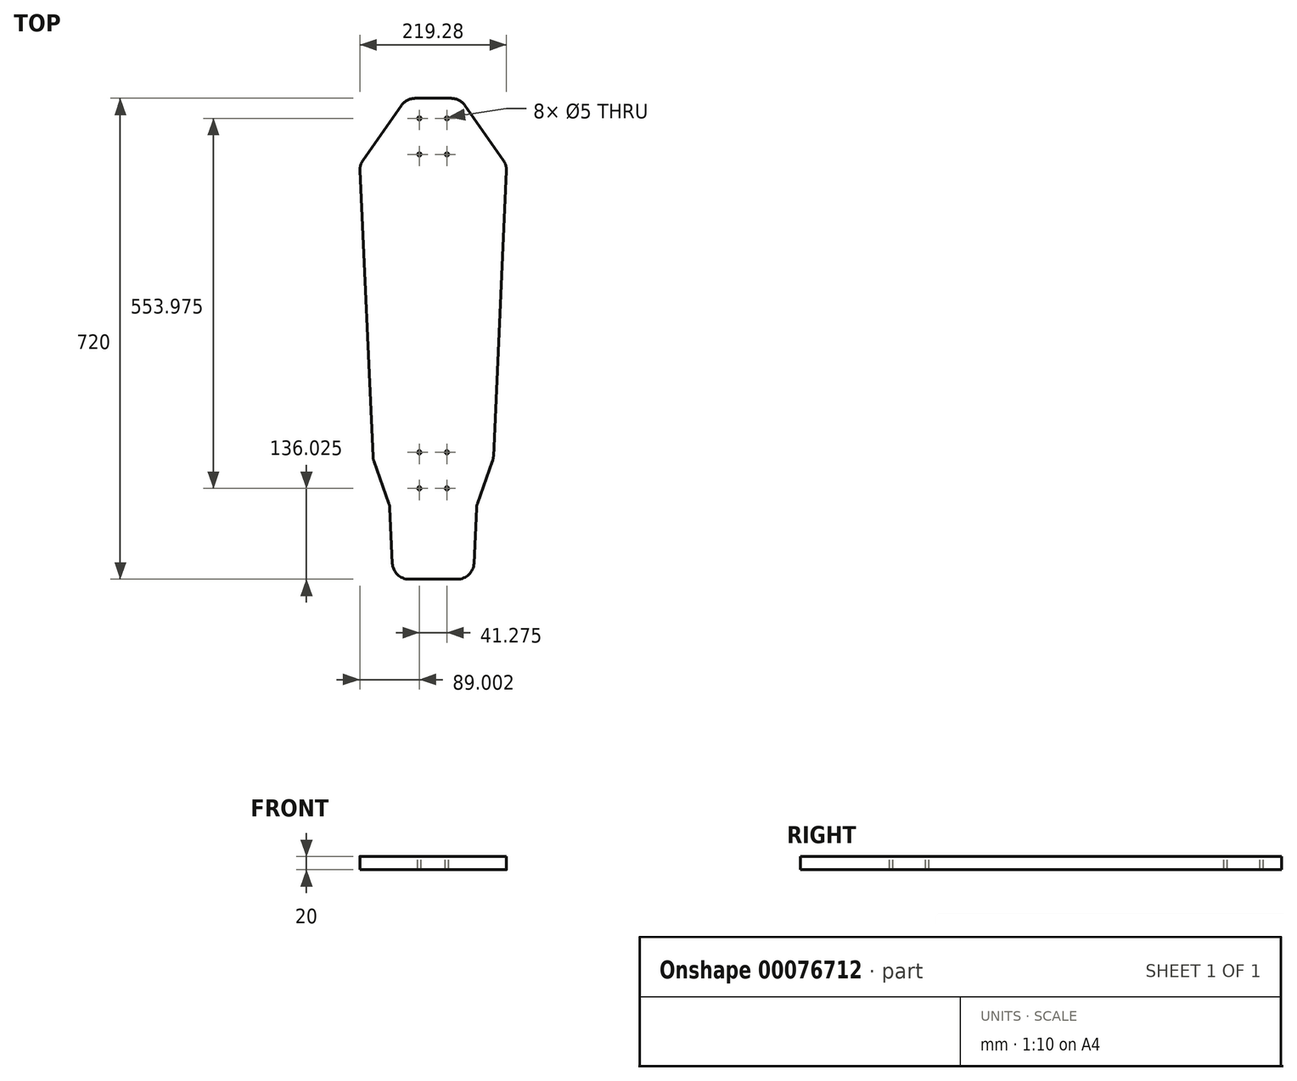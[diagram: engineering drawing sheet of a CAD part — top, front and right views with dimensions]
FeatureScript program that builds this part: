
annotation { "Feature Type Name" : "Feature", "Feature Type Description" : "" }
export const myFeature = defineFeature(function(context is Context, id is Id, definition is map)
    precondition{}
    {
        {
            var Q0;
            Q0=qCreatedBy(makeId("Top.planeOp"),FACE);
            var sketch = newSketch(context, id + "F0", { "sketchPlane" : qUnion([Q0])});
            skLineSegment(sketch, "E0.bottom", {"start": v(-110, 360) * mm, "end": v(110, 360) * mm});
            skLineSegment(sketch, "E0.top", {"start": v(-110, -360) * mm, "end": v(110, -360) * mm});
            skLineSegment(sketch, "E0.left", {"start": v(-110, 360) * mm, "end": v(-110, -360) * mm});
            skLineSegment(sketch, "E0.right", {"start": v(110, 360) * mm, "end": v(110, -360) * mm});
            skPoint(sketch, "E0.middle", {"position": v(0, 0) * mm});
            skLineSegment(sketch, "E1.bottom", {"start": v(-20.64, 330) * mm, "end": v(20.64, 330) * mm, "construction": true});
            skLineSegment(sketch, "E1.top", {"start": v(-20.64, 276.03) * mm, "end": v(20.64, 276.03) * mm, "construction": true});
            skLineSegment(sketch, "E1.left", {"start": v(-20.64, 330) * mm, "end": v(-20.64, 276.03) * mm, "construction": true});
            skLineSegment(sketch, "E1.right", {"start": v(20.64, 330) * mm, "end": v(20.64, 276.03) * mm, "construction": true});
            skLineSegment(sketch, "E2", {"start": v(0, 360) * mm, "end": v(0, -360) * mm});
            skPoint(sketch, "E3", {"position": v(0, 330) * mm});
            skPoint(sketch, "E4", {"position": v(0, 276.03) * mm});
            skLineSegment(sketch, "E5", {"start": v(-20.64, 330) * mm, "end": v(20.64, 276.03) * mm, "construction": true});
            skPoint(sketch, "E6", {"position": v(0, 303.01) * mm});
            skCircle(sketch, "E7", {"center": v(-20.64, 330) * mm, "radius": 2.5 * mm});
            skCircle(sketch, "E8", {"center": v(20.64, 330) * mm, "radius": 2.5 * mm});
            skCircle(sketch, "E9", {"center": v(20.64, 276.03) * mm, "radius": 2.5 * mm});
            skCircle(sketch, "E10", {"center": v(-20.64, 276.03) * mm, "radius": 2.5 * mm});
            skLineSegment(sketch, "E11.bottom", {"start": v(-20.64, -170) * mm, "end": v(20.64, -170) * mm, "construction": true});
            skLineSegment(sketch, "E11.top", {"start": v(-20.64, -223.98) * mm, "end": v(20.64, -223.98) * mm, "construction": true});
            skLineSegment(sketch, "E11.left", {"start": v(-20.64, -170) * mm, "end": v(-20.64, -223.98) * mm, "construction": true});
            skLineSegment(sketch, "E11.right", {"start": v(20.64, -170) * mm, "end": v(20.64, -223.98) * mm, "construction": true});
            skPoint(sketch, "E12", {"position": v(0, -170) * mm});
            skPoint(sketch, "E13", {"position": v(0, -223.98) * mm});
            skLineSegment(sketch, "E14", {"start": v(-20.64, -170) * mm, "end": v(20.64, -223.98) * mm, "construction": true});
            skPoint(sketch, "E15", {"position": v(0, -196.99) * mm});
            skCircle(sketch, "E16", {"center": v(-20.64, -170) * mm, "radius": 2.5 * mm});
            skCircle(sketch, "E17", {"center": v(20.64, -170) * mm, "radius": 2.5 * mm});
            skCircle(sketch, "E18", {"center": v(20.64, -223.98) * mm, "radius": 2.5 * mm});
            skCircle(sketch, "E19", {"center": v(-20.64, -223.98) * mm, "radius": 2.5 * mm});
            skSolve(sketch);
        }
        {
            var Q0;
            Q0=qCreatedBy(makeId("Right.planeOp"),FACE);
            var sketch = newSketch(context, id + "F1", { "sketchPlane" : qUnion([Q0])});
            skLineSegment(sketch, "E20", {"start": v(-180.67, 0) * mm, "end": v(360, 0) * mm});
            skLineSegment(sketch, "E21", {"start": v(-232.43, 6.81) * mm, "end": v(-310, 27.6) * mm});
            skLineSegment(sketch, "E22", {"start": v(-207, 0) * mm, "end": v(-346.12, 0) * mm, "construction": true});
            skPoint(sketch, "E23.visualSharp", {"position": v(-207, 0) * mm});
            skArc(sketch, "E23.filletArc", {"start": v(-232.43, 6.81) * mm, "mid": v(-206.77, 1.71) * mm, "end": v(-180.67, 0) * mm});
            skSolve(sketch);
        }
        {
            var Q0;
            Q0=qSketchRegion(id+"F0",true);
            extrude(context, id + "F2", {"entities" : qUnion([Q0]), "oppositeDirection" : true, "depth" : 20 * mm});
        }
        {
            var Q0;
            Q0=makeQuery(id+"F2.opExtrude","CAP_FACE",FACE,{"disambiguationData":[OSD([sQuery(id+"F0.wireOp",EDGE,"E0.bottom"),sQuery(id+"F0.wireOp",EDGE,"E0.top"),sQuery(id+"F0.wireOp",EDGE,"E0.left"),sQuery(id+"F0.wireOp",EDGE,"E0.right"),sQuery(id+"F0.wireOp",EDGE,"E7"),sQuery(id+"F0.wireOp",EDGE,"E8"),sQuery(id+"F0.wireOp",EDGE,"E9"),sQuery(id+"F0.wireOp",EDGE,"E10"),sQuery(id+"F0.wireOp",EDGE,"E16"),sQuery(id+"F0.wireOp",EDGE,"E17"),sQuery(id+"F0.wireOp",EDGE,"E18"),sQuery(id+"F0.wireOp",EDGE,"E19")])],"isStart":true});
            var sketch = newSketch(context, id + "F3", { "sketchPlane" : qUnion([Q0])});
            skLineSegment(sketch, "E24", {"start": v(-47.46, 349.34) * mm, "end": v(-105.12, 266.97) * mm});
            skLineSegment(sketch, "E25", {"start": v(-109.61, 251.5) * mm, "end": v(-90.17, -176.26) * mm});
            skLineSegment(sketch, "E26", {"start": v(-88.74, -183.53) * mm, "end": v(-66.26, -246.47) * mm});
            skLineSegment(sketch, "E27", {"start": v(-64.83, -253.74) * mm, "end": v(-61.08, -336.14) * mm});
            skPoint(sketch, "E28.visualSharp", {"position": v(-65, -250) * mm});
            skArc(sketch, "E28.filletArc", {"start": v(-64.83, -253.74) * mm, "mid": v(-65.27, -250.05) * mm, "end": v(-66.26, -246.47) * mm});
            skPoint(sketch, "E29.visualSharp", {"position": v(-90, -180) * mm});
            skArc(sketch, "E29.filletArc", {"start": v(-90.17, -176.26) * mm, "mid": v(-89.73, -179.95) * mm, "end": v(-88.74, -183.53) * mm});
            skPoint(sketch, "E30.visualSharp", {"position": v(-110, 260) * mm});
            skArc(sketch, "E30.filletArc", {"start": v(-105.12, 266.97) * mm, "mid": v(-108.65, 259.6) * mm, "end": v(-109.61, 251.5) * mm});
            skLineSegment(sketch, "E31.MirrorCS", {"start": v(47.46, 349.34) * mm, "end": v(105.12, 266.97) * mm});
            skArc(sketch, "E32.MirrorCS", {"start": v(105.12, 266.97) * mm, "mid": v(108.65, 259.6) * mm, "end": v(109.61, 251.5) * mm});
            skLineSegment(sketch, "E33.MirrorCS", {"start": v(109.61, 251.5) * mm, "end": v(90.17, -176.26) * mm});
            skArc(sketch, "E34.MirrorCS", {"start": v(90.17, -176.26) * mm, "mid": v(89.73, -179.95) * mm, "end": v(88.74, -183.53) * mm});
            skLineSegment(sketch, "E35.MirrorCS", {"start": v(88.74, -183.53) * mm, "end": v(66.26, -246.47) * mm});
            skArc(sketch, "E36.MirrorCS", {"start": v(64.83, -253.74) * mm, "mid": v(65.27, -250.05) * mm, "end": v(66.26, -246.47) * mm});
            skLineSegment(sketch, "E37.MirrorCS", {"start": v(64.83, -253.74) * mm, "end": v(61.08, -336.14) * mm});
            skLineSegment(sketch, "E38", {"start": v(-36.11, -360) * mm, "end": v(36.11, -360) * mm});
            skLineSegment(sketch, "E39", {"start": v(-26.98, 360) * mm, "end": v(26.98, 360) * mm});
            skPoint(sketch, "E40.visualSharp", {"position": v(-40, 360) * mm});
            skArc(sketch, "E40.filletArc", {"start": v(-26.98, 360) * mm, "mid": v(-38.53, 357.17) * mm, "end": v(-47.46, 349.34) * mm});
            skPoint(sketch, "E41.visualSharp", {"position": v(40, 360) * mm});
            skArc(sketch, "E41.filletArc", {"start": v(47.46, 349.34) * mm, "mid": v(38.53, 357.17) * mm, "end": v(26.98, 360) * mm});
            skPoint(sketch, "E42.visualSharp", {"position": v(60, -360) * mm});
            skArc(sketch, "E42.filletArc", {"start": v(36.11, -360) * mm, "mid": v(53.38, -353.07) * mm, "end": v(61.08, -336.14) * mm});
            skPoint(sketch, "E43.visualSharp", {"position": v(-60, -360) * mm});
            skArc(sketch, "E43.filletArc", {"start": v(-61.08, -336.14) * mm, "mid": v(-53.38, -353.07) * mm, "end": v(-36.11, -360) * mm});
            skSolve(sketch);
        }
        {
            var Q0;
            Q0=qSketchRegion(id+"F3",true);
            extrude(context, id + "F4", {"entities" : qUnion([Q0]), "operationType" : NewBodyOperationType.INTERSECT, "endBound" : BoundingType.THROUGH_ALL, "oppositeDirection" : true, "depth" : 25 * mm});
        }
    });
